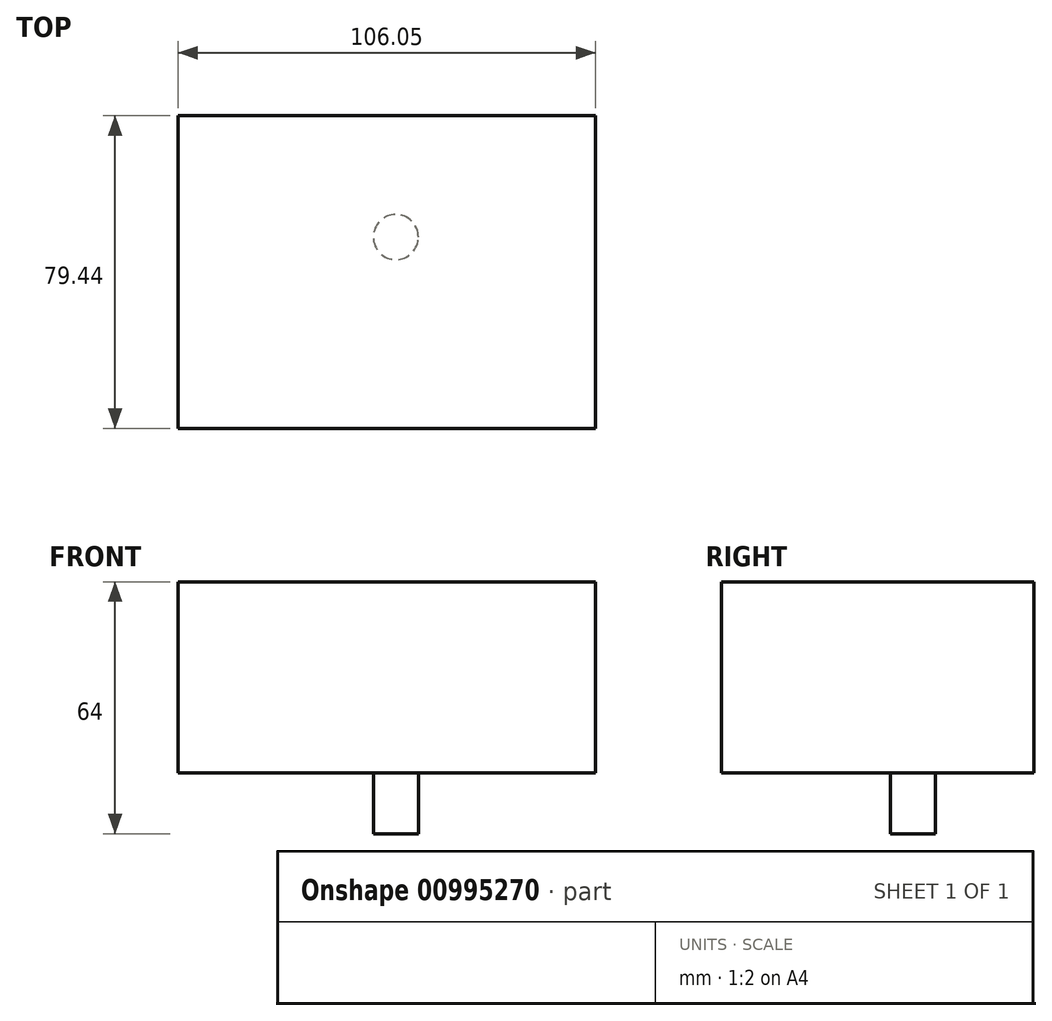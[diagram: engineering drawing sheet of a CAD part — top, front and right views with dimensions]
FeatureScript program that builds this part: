
annotation { "Feature Type Name" : "Feature", "Feature Type Description" : "" }
export const myFeature = defineFeature(function(context is Context, id is Id, definition is map)
    precondition{}
    {
        {
            var Q0;
            Q0=qCreatedBy(makeId("Top.planeOp"),FACE);
            var sketch = newSketch(context, id + "F0", { "sketchPlane" : qUnion([Q0])});
            skLineSegment(sketch, "E0.bottom", {"start": v(-50.49, 34.72) * mm, "end": v(55.56, 34.72) * mm});
            skLineSegment(sketch, "E0.top", {"start": v(-50.49, -44.72) * mm, "end": v(55.56, -44.72) * mm});
            skLineSegment(sketch, "E0.left", {"start": v(-50.49, 34.72) * mm, "end": v(-50.49, -44.72) * mm});
            skLineSegment(sketch, "E0.right", {"start": v(55.56, 34.72) * mm, "end": v(55.56, -44.72) * mm});
            skSolve(sketch);
        }
        {
            var Q0;
            Q0=makeQuery(id+"F0.imprint","IMPRINT",FACE,{"disambiguationData":[TD([[makeQuery(id+"F0.imprint","IMPRINT",EDGE,{"derivedFrom":sQuery(id+"F0.wireOp",EDGE,"E0.bottom")}),-1.0]])]});
            extrude(context, id + "F1", {"entities" : qUnion([Q0]), "depth" : 48.5 * mm, "offsetDistance" : 25.4 * mm});
        }
        {
            var Q0;
            Q0=makeQuery(id+"F1.opExtrude","CAP_FACE",FACE,{"disambiguationData":[OSD([sQuery(id+"F0.wireOp",EDGE,"E0.bottom"),sQuery(id+"F0.wireOp",EDGE,"E0.top"),sQuery(id+"F0.wireOp",EDGE,"E0.left"),sQuery(id+"F0.wireOp",EDGE,"E0.right")])],"isStart":false});
            var sketch = newSketch(context, id + "F2", { "sketchPlane" : qUnion([Q0])});
            skCircle(sketch, "E1", {"center": v(4.83, 3.89) * mm, "radius": 5.72 * mm});
            skSolve(sketch);
        }
        {
            var Q0;
            Q0 = qSketchRegion(id + "F2", true);
            extrude(context, id + "F3", {"entities" : qUnion([Q0]), "operationType" : NewBodyOperationType.ADD, "oppositeDirection" : true, "depth" : 64 * mm, "offsetDistance" : 25.4 * mm});
        }
    });
